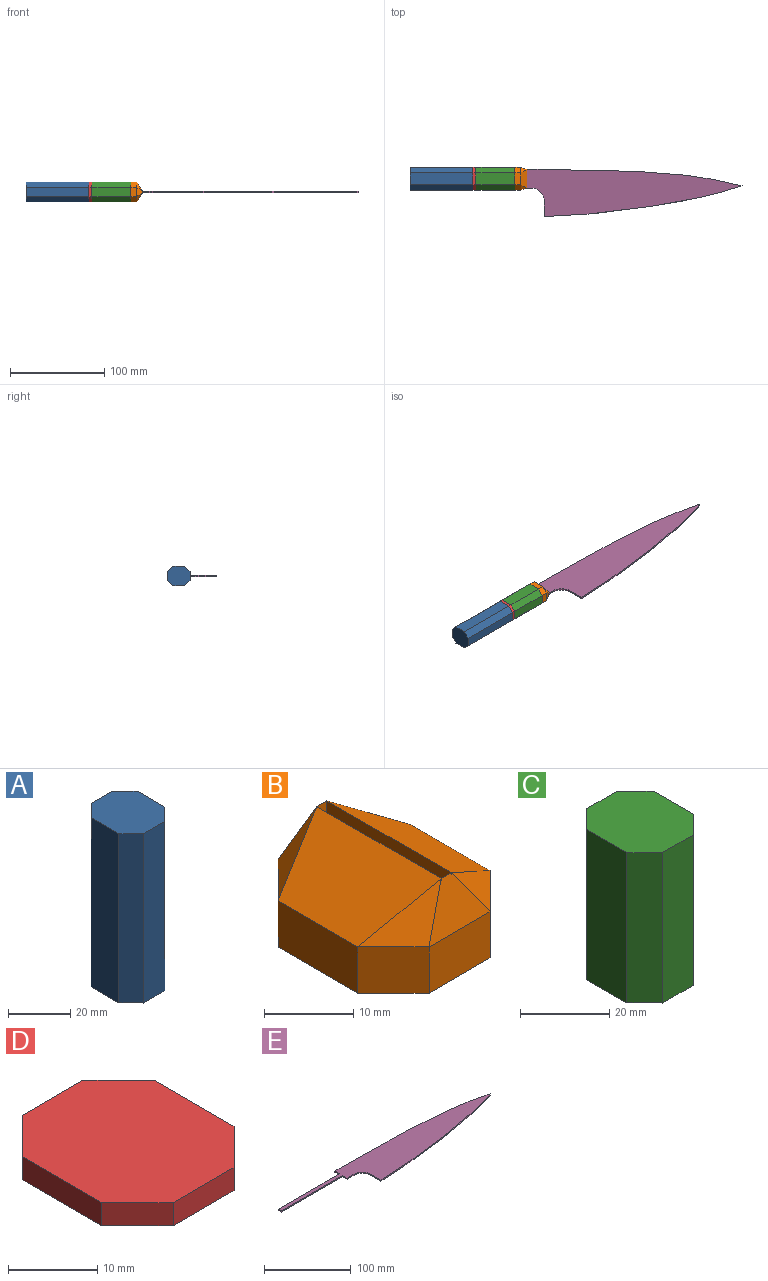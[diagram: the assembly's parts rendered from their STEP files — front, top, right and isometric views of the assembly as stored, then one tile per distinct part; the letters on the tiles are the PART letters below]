
ASSEMBLY  parts=5 mates=5
PART A: 10 faces, bbox 21x24x66.8 mm
  f0: plane 66.75x9.69mm, normal (0,-1,0), area 646.6mm2, adj f1,f7,f8,f9
  f1: plane 66.75x5.66mm, normal (0.71,-0.71,0), area 534mm2, adj f0,f2,f8,f9
  f2: plane 66.75x12.69mm, normal (1,0,0), area 846.8mm2, adj f1,f3,f8,f9
  f3: plane 66.75x5.66mm, normal (0.71,0.71,0), area 534mm2, adj f2,f4,f8,f9
  f4: plane 66.75x9.69mm, normal (0,1,0), area 646.6mm2, adj f3,f5,f8,f9
  f5: plane 66.75x5.66mm, normal (-0.71,0.71,0), area 534mm2, adj f4,f6,f8,f9
  f6: plane 66.75x12.69mm, normal (-1,0,0), area 846.8mm2, adj f5,f7,f8,f9
  f7: plane 66.75x5.66mm, normal (-0.71,-0.71,0), area 534mm2, adj f0,f6,f8,f9
  f8: plane 24x21mm, normal (0,0,1), area 440mm2, adj f0,f1,f2,f3,f4,f5,f6,f7
  f9: plane 24x21mm, normal (0,0,-1), area 440mm2, adj f0,f1,f2,f3,f4,f5,f6,f7
PART B: 25 faces, bbox 21x24x12.7 mm
  f0: plane 7.38x1.59mm, normal (0,0,1), area 11.7mm2, adj f10,f12,f13,f23
  f1: plane 24x21mm, normal (0,0,-1), area 432.1mm2, adj f10,f12,f15,f16,f17,f18,f19,f20
  f2: plane 19.75x9.71mm, normal (-0.55,0,0.84), area 188.1mm2, adj f4,f8,f12,f21
  f3: plane 9.71x6.35mm, normal (0.58,-0.58,0.57), area 30.8mm2, adj f7,f9,f16
  f4: plane 9.71x6.35mm, normal (-0.58,0.58,0.57), area 30.8mm2, adj f2,f5,f20
  f5: plane 9.69x6.35mm, normal (0,0.95,0.32), area 37.8mm2, adj f4,f6,f11,f19
  f6: plane 9.71x6.35mm, normal (0.58,0.58,0.57), area 30.8mm2, adj f5,f7,f18
  f7: plane 19.75x9.71mm, normal (0.55,0,0.84), area 188.1mm2, adj f3,f6,f10,f17
  f8: plane 9.71x6.35mm, normal (-0.58,-0.58,0.57), area 30.8mm2, adj f2,f9,f22
  f9: plane 9.69x6.35mm, normal (0,-0.95,0.32), area 37.8mm2, adj f3,f8,f13,f15
  f10: plane 19.75x12.7mm, normal (-1,0,0), area 157.2mm2, adj f0,f1,f7,f11,f13,f14,f23,f24
  f11: plane 6.35x1.59mm, normal (0,-1,0), area 10.1mm2, adj f5,f10,f12,f14
  f12: plane 19.75x12.7mm, normal (1,0,0), area 157.2mm2, adj f0,f1,f2,f11,f13,f14,f23,f24
  f13: plane 6.35x1.59mm, normal (0,1,0), area 10.1mm2, adj f0,f9,f10,f12
  f14: plane 7.38x1.59mm, normal (0,0,1), area 11.7mm2, adj f10,f11,f12,f24
  f15: plane 9.69x6.35mm, normal (0,-1,0), area 61.5mm2, adj f1,f9,f16,f22
  f16: plane 6.35x5.66mm, normal (0.71,-0.71,0), area 50.8mm2, adj f1,f3,f15,f17
  f17: plane 12.69x6.35mm, normal (1,0,0), area 80.6mm2, adj f1,f7,f16,f18
  f18: plane 6.35x5.66mm, normal (0.71,0.71,0), area 50.8mm2, adj f1,f6,f17,f19
  f19: plane 9.69x6.35mm, normal (0,1,0), area 61.5mm2, adj f1,f5,f18,f20
  f20: plane 6.35x5.66mm, normal (-0.71,0.71,0), area 50.8mm2, adj f1,f4,f19,f21
  f21: plane 12.69x6.35mm, normal (-1,0,0), area 80.6mm2, adj f1,f2,f20,f22
  f22: plane 6.35x5.66mm, normal (-0.71,-0.71,0), area 50.8mm2, adj f1,f8,f15,f21
  f23: plane 6.35x1.59mm, normal (0,1,0), area 10.1mm2, adj f0,f1,f10,f12
  f24: plane 6.35x1.59mm, normal (0,-1,0), area 10.1mm2, adj f1,f10,f12,f14
PART C: 10 faces, bbox 21x24x41.2 mm
  f0: plane 41.2x9.69mm, normal (0,-1,0), area 399.1mm2, adj f1,f7,f8,f9
  f1: plane 41.2x5.66mm, normal (0.71,-0.71,0), area 329.6mm2, adj f0,f2,f8,f9
  f2: plane 41.2x12.69mm, normal (1,0,0), area 522.7mm2, adj f1,f3,f8,f9
  f3: plane 41.2x5.66mm, normal (0.71,0.71,0), area 329.6mm2, adj f2,f4,f8,f9
  f4: plane 41.2x9.69mm, normal (0,1,0), area 399.1mm2, adj f3,f5,f8,f9
  f5: plane 41.2x5.66mm, normal (-0.71,0.71,0), area 329.6mm2, adj f4,f6,f8,f9
  f6: plane 41.2x12.69mm, normal (-1,0,0), area 522.7mm2, adj f5,f7,f8,f9
  f7: plane 41.2x5.66mm, normal (-0.71,-0.71,0), area 329.6mm2, adj f0,f6,f8,f9
  f8: plane 24x21mm, normal (0,0,1), area 440mm2, adj f0,f1,f2,f3,f4,f5,f6,f7
  f9: plane 24x21mm, normal (0,0,-1), area 440mm2, adj f0,f1,f2,f3,f4,f5,f6,f7
PART D: 10 faces, bbox 21x24x3.2 mm
  f0: plane 9.69x3.18mm, normal (0,-1,0), area 30.8mm2, adj f1,f7,f8,f9
  f1: plane 5.66x5.66mm, normal (0.71,-0.71,0), area 25.4mm2, adj f0,f2,f8,f9
  f2: plane 12.69x3.18mm, normal (1,0,0), area 40.3mm2, adj f1,f3,f8,f9
  f3: plane 5.66x5.66mm, normal (0.71,0.71,0), area 25.4mm2, adj f2,f4,f8,f9
  f4: plane 9.69x3.18mm, normal (0,1,0), area 30.8mm2, adj f3,f5,f8,f9
  f5: plane 5.66x5.66mm, normal (-0.71,0.71,0), area 25.4mm2, adj f4,f6,f8,f9
  f6: plane 12.69x3.18mm, normal (-1,0,0), area 40.3mm2, adj f5,f7,f8,f9
  f7: plane 5.66x5.66mm, normal (-0.71,-0.71,0), area 25.4mm2, adj f0,f6,f8,f9
  f8: plane 24x21mm, normal (0,0,1), area 440mm2, adj f0,f1,f2,f3,f4,f5,f6,f7
  f9: plane 24x21mm, normal (0,0,-1), area 440mm2, adj f0,f1,f2,f3,f4,f5,f6,f7
PART E: 31 faces, bbox 337.8x52.7x1.6 mm
  f0: plane 337.81x52.71mm, normal (0,0,-1), area 8107.1mm2, adj f1,f2,f3,f4,f5,f6,f7,f8
  f1: plane 100x1.59mm, normal (0,-1,0), area 159mm2, adj f0,f2,f11,f12
  f2: plane 7.38x1.59mm, normal (-1,0,0), area 11.7mm2, adj f0,f1,f3,f12
  f3: plane 11.35x1.59mm, normal (0,-1,0), area 18mm2, adj f0,f2,f4,f12
  f4: cylinder r=13.5mm len=13.5mm, axis (0,0,-1), area 33.7mm2, adj f0,f3,f5,f12
  f5: plane 16.75x1.59mm, normal (-1,0,0), area 26.6mm2, adj f0,f4,f6,f12
  f6: extruded ~210x32.62mm, area 338.9mm2, adj f0,f5,f7,f12
  f7: extruded ~210x17.38mm, area 336mm2, adj f0,f6,f8,f12
  f8: plane 24.85x1.59mm, normal (0,1,0), area 39.5mm2, adj f0,f7,f9,f12
  f9: plane 7.38x1.59mm, normal (-1,0,0), area 11.7mm2, adj f0,f8,f10,f12
  f10: plane 100x1.59mm, normal (0,1,0), area 159mm2, adj f0,f9,f11,f12
  f11: plane 5x1.59mm, normal (-1,0,0), area 7.9mm2, adj f0,f1,f10,f12
  f12: plane 337.81x52.71mm, normal (0,0,1), area 8157.8mm2, adj f1,f2,f3,f4,f5,f6,f7,f8
  f13: plane 1.92x1.47mm, normal (-0.58,-0.74,-0.34), area 1.2mm2, adj f14,f15,f17,f24,f28
  f14: plane 1.92x1.35mm, normal (0.5,0.8,-0.34), area 1.1mm2, adj f13,f17,f23,f24,f29
  f15: plane 5.5x0.7mm, normal (-0.94,0,-0.34), area 3.9mm2, adj f13,f17,f24,f28
  f16: cone r=3.5mm half-angle=20deg, axis (0,0,1), area 8.1mm2, adj f17,f18,f22,f25,f27,f30
  f17: plane 7.51x0.7mm, normal (0.94,0,-0.34), area 5.1mm2, adj f13,f14,f15,f16,f18,f23,f25,f27
  f18: plane 1.91x1.34mm, normal (-0.5,-0.8,-0.34), area 1.1mm2, adj f16,f17,f25,f30
  f19: plane 1.75x1.23mm, normal (-0.5,-0.8,-0.34), area 0.3mm2, adj f0,f22,f26
  f20: plane 1.75x1.23mm, normal (-0.58,-0.74,-0.34), area 0.3mm2, adj f0,f21,f22
  f21: plane 1.75x1.23mm, normal (0.5,0.8,-0.34), area 0.3mm2, adj f0,f20,f22
  f22: cone r=4mm half-angle=20deg, axis (0,0,-1), area 17.7mm2, adj f0,f16,f19,f20,f21,f24,f26
  f23: plane 2.02x0.7mm, normal (-0.94,0,-0.34), area 1.2mm2, adj f14,f17,f24,f29
  f24: cone r=3.5mm half-angle=20deg, axis (0,0,1), area 8.1mm2, adj f13,f14,f15,f22,f23,f28,f29
  f25: plane 1.91x1.45mm, normal (0.58,0.74,-0.34), area 1.2mm2, adj f16,f17,f18,f27
  f26: plane 1.75x1.23mm, normal (0.58,0.74,-0.34), area 0.3mm2, adj f0,f19,f22
  f27: plane 6.42x3.25mm, normal (0,0,-1), area 15.8mm2, adj f16,f17,f25
  f28: plane 6.42x3.25mm, normal (0,0,-1), area 15.8mm2, adj f13,f15,f24
  f29: plane 1.41x1.3mm, normal (0,0,-1), area 1mm2, adj f14,f23,f24
  f30: plane 1.41x1.3mm, normal (0,0,-1), area 1mm2, adj f16,f17,f18
PLACE A rot(axis=(0,1,0),90deg) t=(-290.86,-51.18,-17.43)mm
PLACE B rot(axis=(0,1,0),90deg) t=(-173.39,-50.95,-17.7)mm
PLACE C rot(axis=(0,-1,0),90deg) t=(-179.74,-48.61,-15.75)mm
PLACE D rot(axis=(0,1,0),90deg) t=(-224.11,-60.43,-26.25)mm
PLACE E t=(-43.54,-66.08,-18.49)mm
MATE planar E.f9 <-> B.f14  axis (-1,0,0) through (-173.39,-44.77,-17.7)mm
MATE fastened D.f8 <-> C.f8  axis (1,0,0) through (-220.94,-50.95,-17.7)mm
MATE fastened A.f8 <-> D.f9  axis (1,0,0) through (-224.11,-50.95,-17.7)mm
MATE slider E.f11 <-> C.f9  axis (-1,0,0) through (-273.39,-50.95,-17.7)mm
MATE fastened C.f9 <-> B.f1  axis (1,0,0) through (-179.74,-50.95,-17.7)mm
